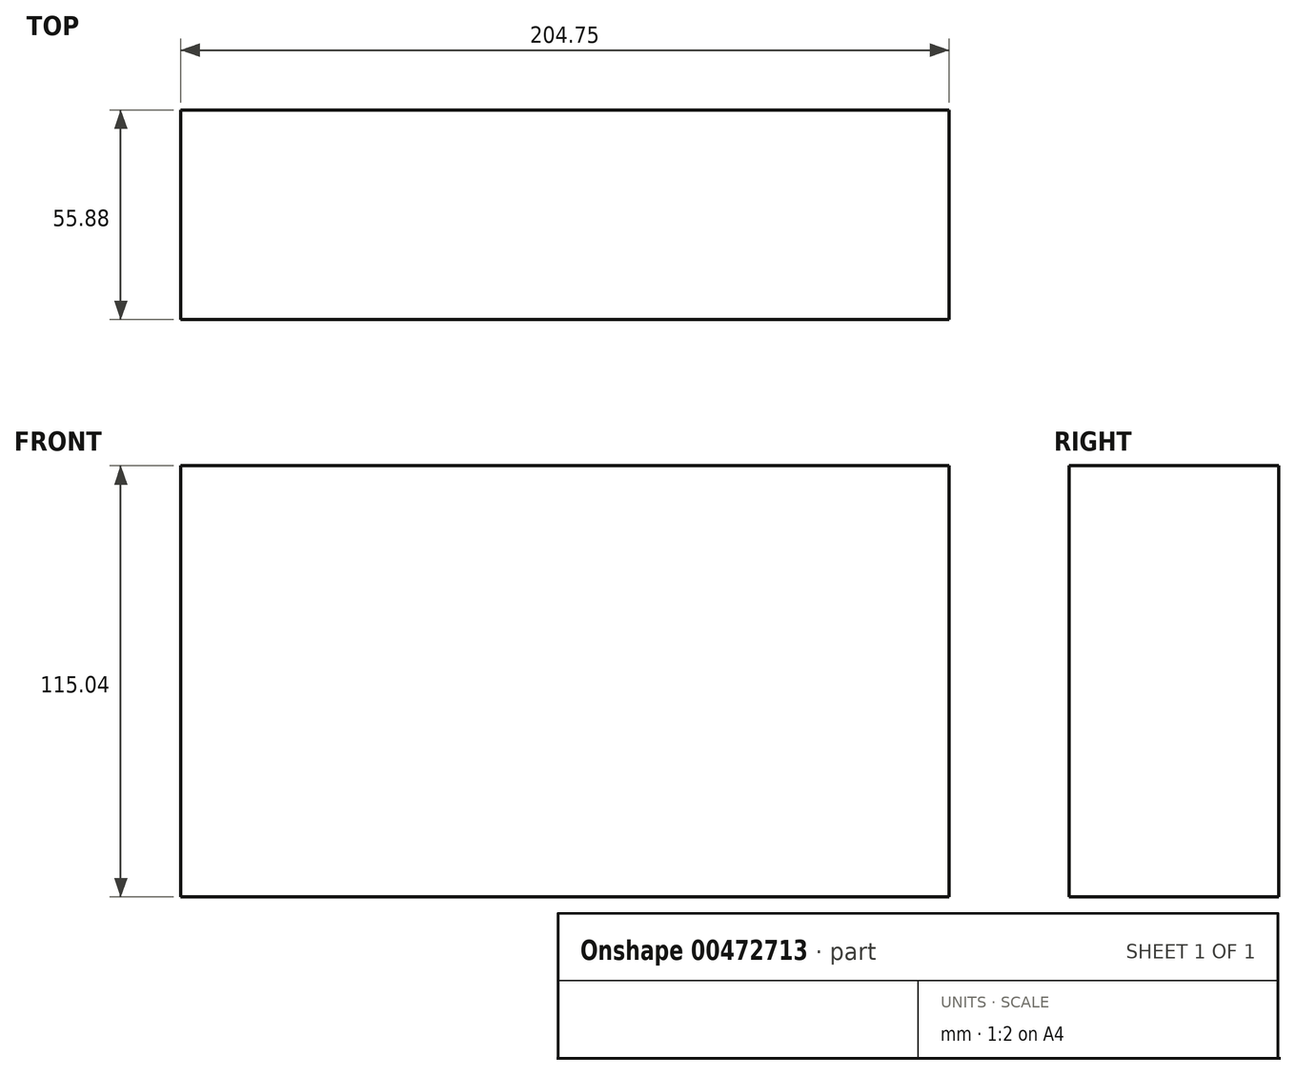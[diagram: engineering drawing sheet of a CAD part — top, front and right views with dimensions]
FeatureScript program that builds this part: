
annotation { "Feature Type Name" : "Feature", "Feature Type Description" : "" }
export const myFeature = defineFeature(function(context is Context, id is Id, definition is map)
    precondition{}
    {
        {
            var Q0;
            Q0=qCreatedBy(makeId("Front.planeOp"),FACE);
            var sketch = newSketch(context, id + "F0", { "sketchPlane" : qUnion([Q0])});
            skLineSegment(sketch, "E0.bottom", {"start": v(-105.18, 55.42) * mm, "end": v(99.57, 55.42) * mm});
            skLineSegment(sketch, "E0.top", {"start": v(-105.18, -59.62) * mm, "end": v(99.57, -59.62) * mm});
            skLineSegment(sketch, "E0.left", {"start": v(-105.18, 55.42) * mm, "end": v(-105.18, -59.62) * mm});
            skLineSegment(sketch, "E0.right", {"start": v(99.57, 55.42) * mm, "end": v(99.57, -59.62) * mm});
            skSolve(sketch);
        }
        {
            var Q0;
            Q0 = qSketchRegion(id + "F0", true);
            extrude(context, id + "F1", {"entities" : qUnion([Q0]), "oppositeDirection" : true, "depth" : 55.88 * mm});
        }
    });
